# Revit family: HERZ-Design-Thermostatic Sensor M28x1.5 9260
name_source: partatom
category: Rohrzubehör
revit_build: Autodesk Revit 2018 (Build: 20190510_1515(x64)
units: mm (PartAtom-declared; Revit-internal decimal feet)

## family parameters
Arbeitsebenenbasiert = Nein
Beim Laden mit Abzugskörper schneiden = Nein
Bemaßung runder Anschluss = Durchmesser verwenden
Gemeinsam genutzt = Nein
Immer vertikal = Nein
OmniClass-Nummer = 23.65.55.14
OmniClass-Titel = Valves for Liquid Services
Teiletyp = Normal

## types (1)
- HERZ-Design-Thermostatic Sensor M28x1.5 9260
    Application = Can be combined with any HERZ-valve suitable for thermostatic operation.
    Finish = Radiator Thermostat With Hydrosensor (liquid filled)
With automatic frost release, limitation and locking of selected temperature range,
handwheel white.
    Frost protection = 6 °C
    Hand wheel = plastic, white
    Hersteller = HERZ Armaturen Ges.m.b.H.
    Operation = The HERZ thermostat serves as a room temperature sensing and control unit.
The change in volume of the liquid contained in the hydrosensor actuates the valve spindle.
    Part number = 1926006
    S01 = 90 mm  [stored 0.295276 ft]
    S02 = 60 mm  [stored 0.19685 ft]
    Set value range = 6-28°C
    URL = www.herzvalves.com

note: [stored X ft] marks values corroborated as IEEE doubles in the binary element streams (Revit-internal decimal feet)
